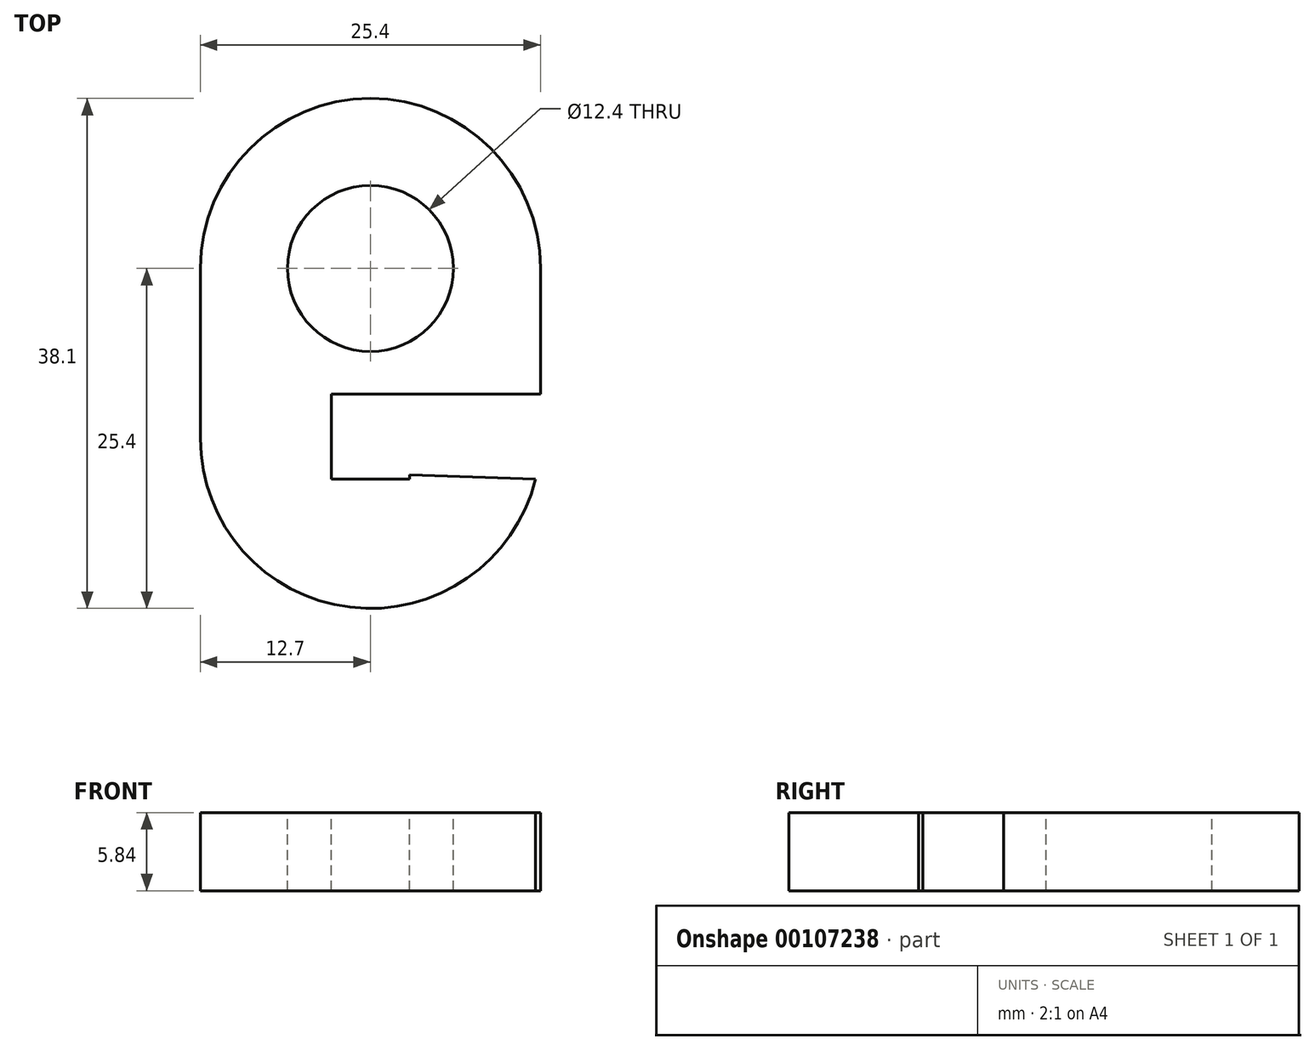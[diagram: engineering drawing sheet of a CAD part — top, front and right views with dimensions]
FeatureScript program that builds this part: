
annotation { "Feature Type Name" : "Feature", "Feature Type Description" : "" }
export const myFeature = defineFeature(function(context is Context, id is Id, definition is map)
    precondition{}
    {
        {
            var Q0;
            Q0=qCreatedBy(makeId("Top.planeOp"),FACE);
            var sketch = newSketch(context, id + "F0", { "sketchPlane" : qUnion([Q0])});
            skCircle(sketch, "E0", {"center": v(0, 0) * mm, "radius": 6.2 * mm});
            skCircle(sketch, "E1", {"center": v(0, 0) * mm, "radius": 12.7 * mm});
            skPoint(sketch, "E2", {"position": v(-12.7, 0) * mm});
            skLineSegment(sketch, "E3", {"start": v(-12.7, 0) * mm, "end": v(-12.7, -12.7) * mm});
            skArc(sketch, "E4", {"start": v(-12.7, -12.7) * mm, "mid": v(0, -25.4) * mm, "end": v(12.7, -12.7) * mm});
            skPoint(sketch, "E5", {"position": v(12.7, 0) * mm});
            skLineSegment(sketch, "E6", {"start": v(12.7, -12.7) * mm, "end": v(12.7, 0) * mm});
            skSolve(sketch);
        }
        {
            var Q0;
            Q0=makeQuery(id+"F0.imprint","IMPRINT",FACE,{"disambiguationData":[TD([[makeQuery(id+"F0.imprint","IMPRINT",EDGE,{"derivedFrom":sQuery(id+"F0.wireOp",EDGE,"E0")}),-1.0]])]});
            var Q1;
            {var subQ0=sQuery(id+"F0.wireOp",EDGE,"E3");Q1=makeQuery(id+"F0.imprint","IMPRINT",FACE,{"disambiguationData":[TD([[makeQuery(id+"F0.imprint","IMPRINT",EDGE,{"derivedFrom":subQ0}),1.0]])]});}
            extrude(context, id + "F1", {"entities" : qUnion([Q0, Q1]), "oppositeDirection" : true, "depth" : 5.84 * mm});
        }
        {
            var Q0;
            Q0=makeQuery(id+"F1.opExtrude","CAP_FACE",FACE,{"disambiguationData":[OSD([sQuery(id+"F0.wireOp",EDGE,"E0"),sQuery(id+"F0.wireOp",EDGE,"E1"),sQuery(id+"F0.wireOp",EDGE,"E3"),sQuery(id+"F0.wireOp",EDGE,"E4"),sQuery(id+"F0.wireOp",EDGE,"E6")])],"isStart":true});
            var sketch = newSketch(context, id + "F2", { "sketchPlane" : qUnion([Q0])});
            skPoint(sketch, "E7", {"position": v(0, -6.2) * mm});
            skPoint(sketch, "E8", {"position": v(-2.92, -9.37) * mm});
            skPoint(sketch, "E9", {"position": v(-2.92, -15.72) * mm});
            skLineSegment(sketch, "E10", {"start": v(-2.92, -9.37) * mm, "end": v(-2.92, -15.72) * mm});
            skLineSegment(sketch, "E11", {"start": v(-2.92, -9.37) * mm, "end": v(12.7, -9.37) * mm});
            skLineSegment(sketch, "E12", {"start": v(-2.92, -15.72) * mm, "end": v(12.34, -15.72) * mm});
            skLineSegment(sketch, "E13", {"start": v(12.34, -15.72) * mm, "end": v(2.92, -15.4) * mm});
            skPoint(sketch, "E14", {"position": v(-2.92, 0) * mm});
            skLineSegment(sketch, "E15", {"start": v(2.92, -15.4) * mm, "end": v(2.92, -15.72) * mm});
            skPoint(sketch, "E16", {"position": v(0, -25.4) * mm});
            skSolve(sketch);
        }
        {
            var Q0;
            {var subQ4=sQuery(id+"F2.wireOp",EDGE,"LBMHB6HF-EqNs-7Qwt-jW4y-MxuY962zRnmd.top");Q0=makeQuery(id+"F2.imprint","IMPRINT",FACE,{"disambiguationData":[TD([[makeQuery(id+"F2.imprint","IMPRINT",EDGE,{"derivedFrom":subQ4}),1.0]])]});}
            var Q1;
            {var subQ0=sQuery(id+"F2.wireOp",EDGE,"LBMHB6HF-EqNs-7Qwt-jW4y-MxuY962zRnmd.right");Q1=makeQuery(id+"F2.imprint","IMPRINT",FACE,{"disambiguationData":[TD([[makeQuery(id+"F2.imprint","IMPRINT",EDGE,{"derivedFrom":subQ0}),-1.0]])]});}
            var Q2;
            {var subQ2=sQuery(id+"F2.wireOp",EDGE,"LBMHB6HF-EqNs-7Qwt-jW4y-MxuY962zRnmd.right");Q2=makeQuery(id+"F2.imprint","IMPRINT",FACE,{"disambiguationData":[TD([[makeQuery(id+"F2.imprint","IMPRINT",EDGE,{"derivedFrom":subQ2}),1.0]])]});}
            var Q3;
            {var subQ6=sQuery(id+"F2.wireOp",EDGE,"p5e3qVRe-jRCM-jpVH-BA4D-DKAgyKM8tcfW.top");Q3=makeQuery(id+"F2.imprint","IMPRINT",FACE,{"disambiguationData":[TD([[makeQuery(id+"F2.imprint","IMPRINT",EDGE,{"derivedFrom":subQ6}),1.0]])]});}
            var Q4;
            Q4=makeQuery(id+"F2.imprint","IMPRINT",FACE,{"disambiguationData":[TD([[makeQuery(id+"F2.imprint","IMPRINT",EDGE,{"derivedFrom":sQuery(id+"F2.wireOp",EDGE,"E10")}),1.0]])]});
            var Q5;
            Q5=makeQuery(id+"F1.opExtrude","CAP_FACE",FACE,{"disambiguationData":[OSD([sQuery(id+"F0.wireOp",EDGE,"E0"),sQuery(id+"F0.wireOp",EDGE,"E1"),sQuery(id+"F0.wireOp",EDGE,"E3"),sQuery(id+"F0.wireOp",EDGE,"E4"),sQuery(id+"F0.wireOp",EDGE,"E6")])],"isStart":false});
            extrude(context, id + "F3", {"entities" : qUnion([Q0, Q1, Q2, Q3, Q4]), "operationType" : NewBodyOperationType.REMOVE, "endBound" : BoundingType.UP_TO_SURFACE, "oppositeDirection" : true, "endBoundEntityFace" : qUnion([Q5]), "depth" : 25.4 * mm});
        }
    });
